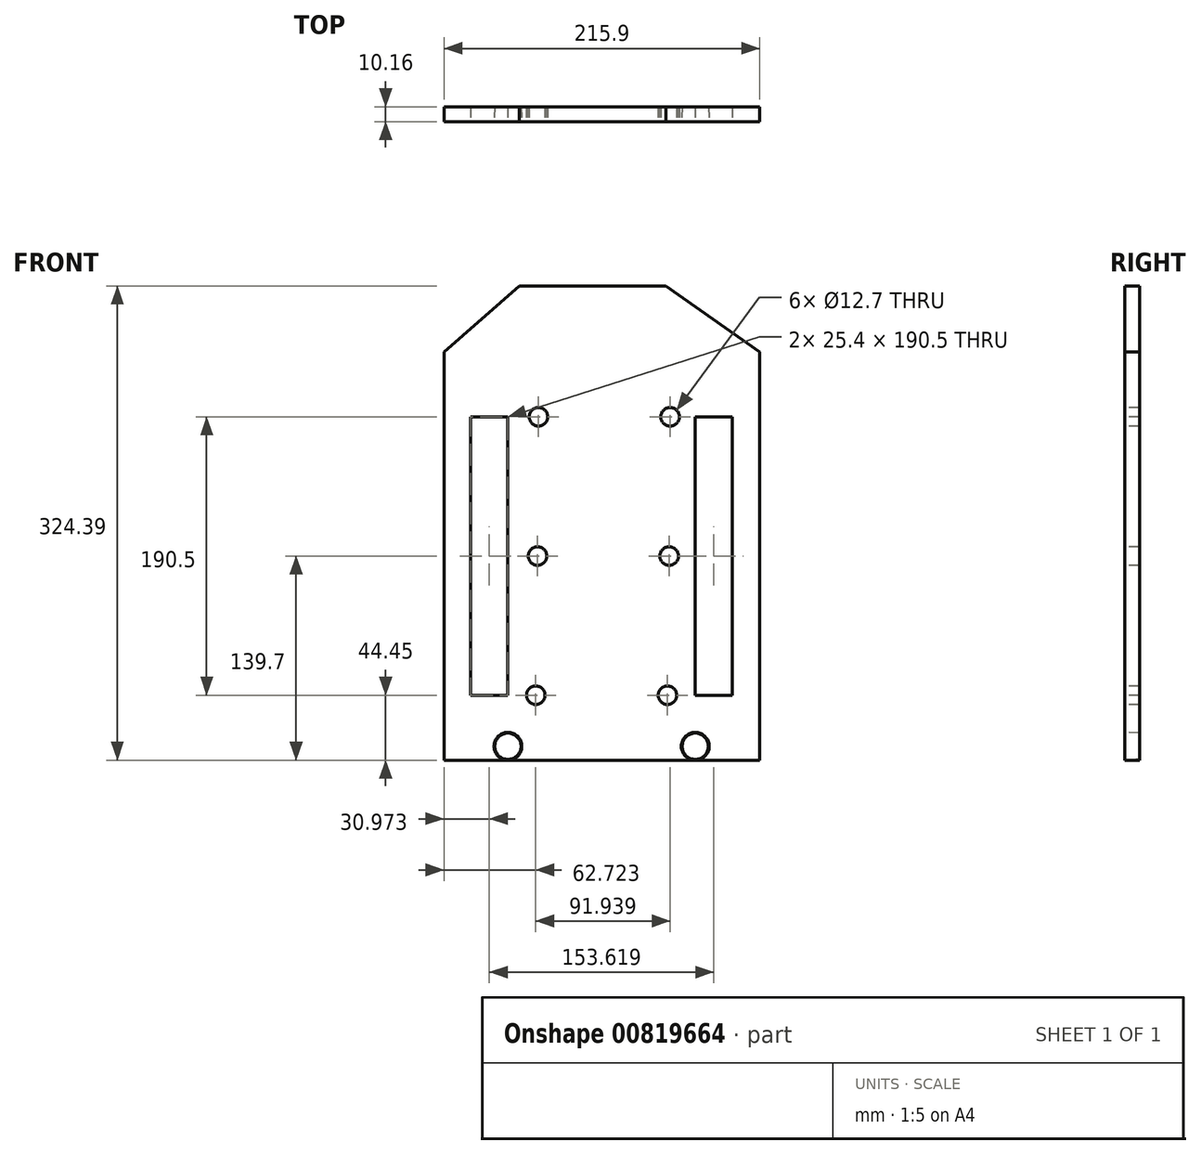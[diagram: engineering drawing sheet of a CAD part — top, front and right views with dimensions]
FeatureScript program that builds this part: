
annotation { "Feature Type Name" : "Feature", "Feature Type Description" : "" }
export const myFeature = defineFeature(function(context is Context, id is Id, definition is map)
    precondition{}
    {
        {
            var Q0;
            Q0=qCreatedBy(makeId("Front.planeOp"),FACE);
            var sketch = newSketch(context, id + "F0", { "sketchPlane" : qUnion([Q0])});
            skLineSegment(sketch, "E0.bottom", {"start": v(107.95, 139.7) * mm, "end": v(-107.95, 139.7) * mm});
            skLineSegment(sketch, "E0.top", {"start": v(107.95, -139.7) * mm, "end": v(-107.95, -139.7) * mm});
            skLineSegment(sketch, "E0.left", {"start": v(107.95, 139.7) * mm, "end": v(107.95, -139.7) * mm});
            skLineSegment(sketch, "E0.right", {"start": v(-107.95, 139.7) * mm, "end": v(-107.95, -139.7) * mm});
            skPoint(sketch, "E0.middle", {"position": v(0, 0) * mm});
            skSolve(sketch);
        }
        {
            var Q0;
            Q0=makeQuery(id+"F0.imprint","IMPRINT",FACE,{"disambiguationData":[TD([[makeQuery(id+"F0.imprint","IMPRINT",EDGE,{"derivedFrom":sQuery(id+"F0.wireOp",EDGE,"E0.bottom")}),1.0]])]});
            extrude(context, id + "F1", {"entities" : qUnion([Q0]), "depth" : 10.16 * mm, "offsetDistance" : 25.4 * mm});
        }
        {
            var Q0;
            Q0=makeQuery(id+"F1.opExtrude","CAP_FACE",FACE,{"disambiguationData":[OSD([sQuery(id+"F0.wireOp",EDGE,"E0.bottom"),sQuery(id+"F0.wireOp",EDGE,"E0.top"),sQuery(id+"F0.wireOp",EDGE,"E0.left"),sQuery(id+"F0.wireOp",EDGE,"E0.right")])],"isStart":false});
            var sketch = newSketch(context, id + "F2", { "sketchPlane" : qUnion([Q0])});
            skLineSegment(sketch, "E1", {"start": v(-107.95, 139.7) * mm, "end": v(107.95, 139.7) * mm});
            skLineSegment(sketch, "E2", {"start": v(107.95, 139.7) * mm, "end": v(43.72, 184.69) * mm});
            skLineSegment(sketch, "E3", {"start": v(43.72, 184.69) * mm, "end": v(-56.53, 184.69) * mm});
            skLineSegment(sketch, "E4", {"start": v(-56.53, 184.69) * mm, "end": v(-107.95, 139.7) * mm});
            skSolve(sketch);
        }
        {
            var Q0;
            Q0=makeQuery(id+"F2.imprint","IMPRINT",FACE,{"disambiguationData":[TD([[makeQuery(id+"F2.imprint","IMPRINT",EDGE,{"derivedFrom":sQuery(id+"F2.wireOp",EDGE,"E1")}),-1.0]])]});
            var Q1;
            Q1 = qSketchRegion(id + "F2", true);
            extrude(context, id + "F3", {"entities" : qUnion([Q0, Q1]), "operationType" : NewBodyOperationType.ADD, "oppositeDirection" : true, "depth" : 10.16 * mm, "offsetDistance" : 25.4 * mm});
        }
        {
            var Q0;
            Q0=makeQuery(id+"F3.boolean.opBoolean","MERGE",FACE,{"derivedFrom":[makeQuery(id+"F1.opExtrude","CAP_FACE",FACE,{"disambiguationData":[OSD([sQuery(id+"F0.wireOp",EDGE,"E0.bottom"),sQuery(id+"F0.wireOp",EDGE,"E0.top"),sQuery(id+"F0.wireOp",EDGE,"E0.left"),sQuery(id+"F0.wireOp",EDGE,"E0.right")])],"isStart":false}),makeQuery(id+"F3.opExtrude","CAP_FACE",FACE,{"disambiguationData":[OSD([sQuery(id+"F2.wireOp",EDGE,"E1"),sQuery(id+"F2.wireOp",EDGE,"E2"),sQuery(id+"F2.wireOp",EDGE,"E3"),sQuery(id+"F2.wireOp",EDGE,"E4")])],"isStart":true})]});
            var sketch = newSketch(context, id + "F4", { "sketchPlane" : qUnion([Q0])});
            skLineSegment(sketch, "E5.bottom", {"start": v(-89.68, -95.25) * mm, "end": v(-64.28, -95.25) * mm});
            skLineSegment(sketch, "E5.top", {"start": v(-89.68, 95.25) * mm, "end": v(-64.28, 95.25) * mm});
            skLineSegment(sketch, "E5.left", {"start": v(-89.68, -95.25) * mm, "end": v(-89.68, 95.25) * mm});
            skLineSegment(sketch, "E5.right", {"start": v(-64.28, -95.25) * mm, "end": v(-64.28, 95.25) * mm});
            skPoint(sketch, "E5.middle", {"position": v(-76.98, 0) * mm});
            skLineSegment(sketch, "E6.bottom", {"start": v(89.34, -95.25) * mm, "end": v(63.94, -95.25) * mm});
            skLineSegment(sketch, "E6.top", {"start": v(89.34, 95.25) * mm, "end": v(63.94, 95.25) * mm});
            skLineSegment(sketch, "E6.left", {"start": v(89.34, -95.25) * mm, "end": v(89.34, 95.25) * mm});
            skLineSegment(sketch, "E6.right", {"start": v(63.94, -95.25) * mm, "end": v(63.94, 95.25) * mm});
            skPoint(sketch, "E6.middle", {"position": v(76.64, 0) * mm});
            skSolve(sketch);
        }
        {
            var Q0;
            Q0=makeQuery(id+"F4.imprint","IMPRINT",FACE,{"disambiguationData":[TD([[makeQuery(id+"F4.imprint","IMPRINT",EDGE,{"derivedFrom":sQuery(id+"F4.wireOp",EDGE,"E5.bottom")}),1.0]])]});
            var Q1;
            Q1=makeQuery(id+"F4.imprint","IMPRINT",FACE,{"disambiguationData":[TD([[makeQuery(id+"F4.imprint","IMPRINT",EDGE,{"derivedFrom":sQuery(id+"F4.wireOp",EDGE,"E6.bottom")}),-1.0]])]});
            extrude(context, id + "F5", {"entities" : qUnion([Q0, Q1]), "operationType" : NewBodyOperationType.REMOVE, "oppositeDirection" : true, "depth" : 25.4 * mm, "offsetDistance" : 25.4 * mm});
        }
        {
            var Q0;
            Q0=makeQuery(id+"F3.boolean.opBoolean","MERGE",FACE,{"derivedFrom":[makeQuery(id+"F1.opExtrude","CAP_FACE",FACE,{"disambiguationData":[OSD([sQuery(id+"F0.wireOp",EDGE,"E0.bottom"),sQuery(id+"F0.wireOp",EDGE,"E0.top"),sQuery(id+"F0.wireOp",EDGE,"E0.left"),sQuery(id+"F0.wireOp",EDGE,"E0.right")])],"isStart":false}),makeQuery(id+"F3.opExtrude","CAP_FACE",FACE,{"disambiguationData":[OSD([sQuery(id+"F2.wireOp",EDGE,"E1"),sQuery(id+"F2.wireOp",EDGE,"E2"),sQuery(id+"F2.wireOp",EDGE,"E3"),sQuery(id+"F2.wireOp",EDGE,"E4")])],"isStart":true})]});
            var sketch = newSketch(context, id + "F6", { "sketchPlane" : qUnion([Q0])});
            skCircle(sketch, "E7", {"center": v(-43.4, 95.25) * mm, "radius": 6.35 * mm});
            skCircle(sketch, "E8", {"center": v(-44.06, 0) * mm, "radius": 6.35 * mm});
            skPoint(sketch, "E8.centerSnap0", {"position": v(-64.28, 0) * mm});
            skCircle(sketch, "E9", {"center": v(-45.23, -95.25) * mm, "radius": 6.35 * mm});
            skCircle(sketch, "E10", {"center": v(46.71, 95.25) * mm, "radius": 6.35 * mm});
            skCircle(sketch, "E11", {"center": v(46.05, 0) * mm, "radius": 6.35 * mm});
            skCircle(sketch, "E12", {"center": v(44.9, -95.25) * mm, "radius": 6.35 * mm});
            skSolve(sketch);
        }
        {
            var Q0;
            Q0=makeQuery(id+"F6.imprint","IMPRINT",FACE,{"disambiguationData":[TD([[makeQuery(id+"F6.imprint","IMPRINT",EDGE,{"derivedFrom":sQuery(id+"F6.wireOp",EDGE,"E7")}),1.0]])]});
            var Q1;
            Q1=makeQuery(id+"F6.imprint","IMPRINT",FACE,{"disambiguationData":[TD([[makeQuery(id+"F6.imprint","IMPRINT",EDGE,{"derivedFrom":sQuery(id+"F6.wireOp",EDGE,"E8")}),1.0]])]});
            var Q2;
            Q2=makeQuery(id+"F6.imprint","IMPRINT",FACE,{"disambiguationData":[TD([[makeQuery(id+"F6.imprint","IMPRINT",EDGE,{"derivedFrom":sQuery(id+"F6.wireOp",EDGE,"E9")}),1.0]])]});
            var Q3;
            Q3=makeQuery(id+"F6.imprint","IMPRINT",FACE,{"disambiguationData":[TD([[makeQuery(id+"F6.imprint","IMPRINT",EDGE,{"derivedFrom":sQuery(id+"F6.wireOp",EDGE,"E10")}),1.0]])]});
            var Q4;
            Q4=makeQuery(id+"F6.imprint","IMPRINT",FACE,{"disambiguationData":[TD([[makeQuery(id+"F6.imprint","IMPRINT",EDGE,{"derivedFrom":sQuery(id+"F6.wireOp",EDGE,"E11")}),1.0]])]});
            var Q5;
            Q5=makeQuery(id+"F6.imprint","IMPRINT",FACE,{"disambiguationData":[TD([[makeQuery(id+"F6.imprint","IMPRINT",EDGE,{"derivedFrom":sQuery(id+"F6.wireOp",EDGE,"E12")}),1.0]])]});
            extrude(context, id + "F7", {"entities" : qUnion([Q0, Q1, Q2, Q3, Q4, Q5]), "operationType" : NewBodyOperationType.REMOVE, "oppositeDirection" : true, "depth" : 25.4 * mm, "offsetDistance" : 25.4 * mm});
        }
        {
            var Q0;
            Q0=makeQuery(id+"F3.boolean.opBoolean","MERGE",FACE,{"derivedFrom":[makeQuery(id+"F1.opExtrude","CAP_FACE",FACE,{"disambiguationData":[OSD([sQuery(id+"F0.wireOp",EDGE,"E0.bottom"),sQuery(id+"F0.wireOp",EDGE,"E0.top"),sQuery(id+"F0.wireOp",EDGE,"E0.left"),sQuery(id+"F0.wireOp",EDGE,"E0.right")])],"isStart":false}),makeQuery(id+"F3.opExtrude","CAP_FACE",FACE,{"disambiguationData":[OSD([sQuery(id+"F2.wireOp",EDGE,"E1"),sQuery(id+"F2.wireOp",EDGE,"E2"),sQuery(id+"F2.wireOp",EDGE,"E3"),sQuery(id+"F2.wireOp",EDGE,"E4")])],"isStart":true})]});
            var sketch = newSketch(context, id + "F8", { "sketchPlane" : qUnion([Q0])});
            skCircle(sketch, "E13", {"center": v(-64.28, -130.18) * mm, "radius": 9.53 * mm});
            skCircle(sketch, "E14", {"center": v(63.94, -130.18) * mm, "radius": 9.53 * mm});
            skSolve(sketch);
        }
        {
            var Q0;
            Q0=makeQuery(id+"F8.imprint","IMPRINT",FACE,{"disambiguationData":[TD([[makeQuery(id+"F8.imprint","IMPRINT",EDGE,{"derivedFrom":sQuery(id+"F8.wireOp",EDGE,"E13")}),1.0]])]});
            var Q1;
            Q1=makeQuery(id+"F8.imprint","IMPRINT",FACE,{"disambiguationData":[TD([[makeQuery(id+"F8.imprint","IMPRINT",EDGE,{"derivedFrom":sQuery(id+"F8.wireOp",EDGE,"E14")}),1.0]])]});
            extrude(context, id + "F9", {"entities" : qUnion([Q0, Q1]), "operationType" : NewBodyOperationType.REMOVE, "oppositeDirection" : true, "depth" : 25.4 * mm, "offsetDistance" : 25.4 * mm, "hasDraft" : true, "draftAngle" : 3 * degree, "draftPullDirection" : true});
        }
    });
